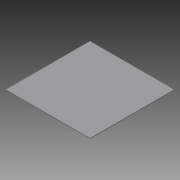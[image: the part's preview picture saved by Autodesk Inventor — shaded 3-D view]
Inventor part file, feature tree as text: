
AUTODESK INVENTOR PART (.ipt)
format: ipt  version: 2014 (Build 180170000, 170)  size: 67,584 bytes
history: native  units: in
note: dims shown in document units (in); Inventor stores cm internally (conversion verified against a paired STEP export)
features: extrude x1, sketch x1
ambient origin geometry x8: Origin, YZ Plane, XZ Plane, XY Plane, X Axis, Y Axis, Z Axis, Center Point
bodies: Solid1 (feature_tree)
feature tree (2):
  extrude  "Extrusion1"  Depth=120.0in
  sketch  "Sketch1"  dims[d0=120.0in d1=120.0in d2=1.0in d3=0.0in]
